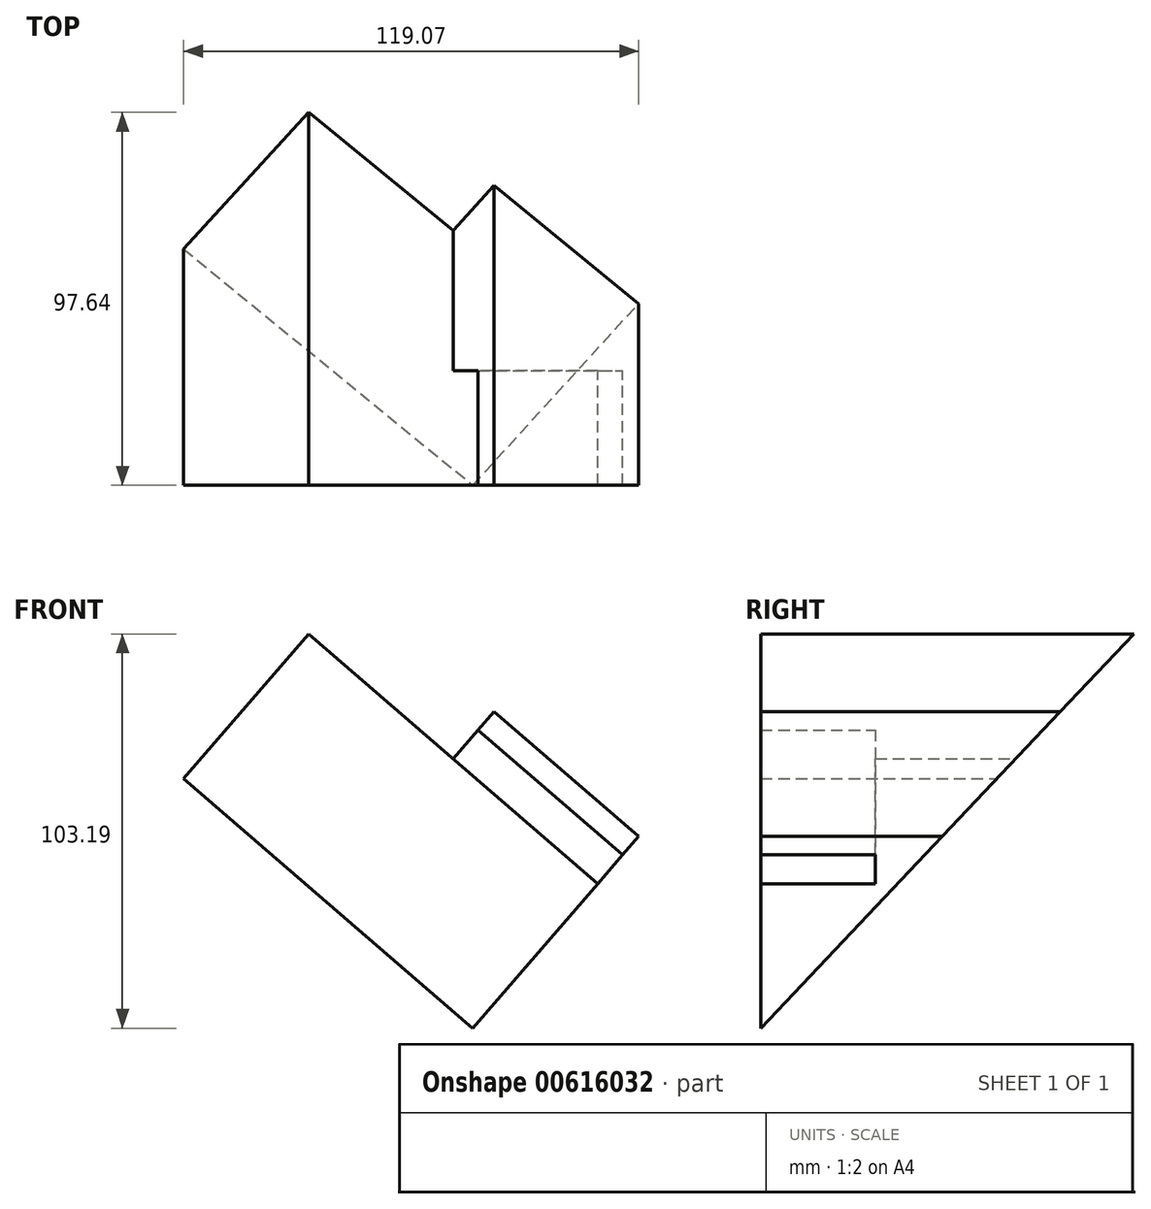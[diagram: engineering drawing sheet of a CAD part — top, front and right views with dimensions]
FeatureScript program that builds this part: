
annotation { "Feature Type Name" : "Feature", "Feature Type Description" : "" }
export const myFeature = defineFeature(function(context is Context, id is Id, definition is map)
    precondition{}
    {
        {
            var Q0;
            Q0=qCreatedBy(makeId("Front.planeOp"),FACE);
            var sketch = newSketch(context, id + "F0", { "sketchPlane" : qUnion([Q0])});
            skLineSegment(sketch, "E0", {"start": v(-8.52, -45.28) * mm, "end": v(24.15, -7.43) * mm});
            skLineSegment(sketch, "E1", {"start": v(24.15, -7.43) * mm, "end": v(-51.55, 57.91) * mm});
            skLineSegment(sketch, "E2", {"start": v(-51.55, 57.91) * mm, "end": v(-84.22, 20.06) * mm});
            skLineSegment(sketch, "E3", {"start": v(-84.22, 20.06) * mm, "end": v(-8.52, -45.28) * mm});
            skLineSegment(sketch, "E4.MirrorCS", {"start": v(47.02, 19.07) * mm, "end": v(30.69, 0.14) * mm});
            skLineSegment(sketch, "E5", {"start": v(44.43, 54.33) * mm, "end": v(44.43, 54.33) * mm});
            skLineSegment(sketch, "E6", {"start": v(9.17, 51.74) * mm, "end": v(-7.16, 32.81) * mm});
            skLineSegment(sketch, "E7", {"start": v(-7.16, 32.81) * mm, "end": v(30.69, 0.14) * mm});
            skPoint(sketch, "E8.visualSharp", {"position": v(25.5, 70.66) * mm});
            skArc(sketch, "E8.filletArc", {"start": v(44.43, 54.33) * mm, "mid": v(26.26, 60.34) * mm, "end": v(9.17, 51.74) * mm});
            skPoint(sketch, "E9.visualSharp", {"position": v(63.36, 38) * mm});
            skArc(sketch, "E9.filletArc", {"start": v(47.02, 19.07) * mm, "mid": v(53.03, 37.23) * mm, "end": v(44.43, 54.33) * mm});
            skLineSegment(sketch, "E10", {"start": v(24.15, -7.43) * mm, "end": v(34.85, 4.96) * mm});
            skLineSegment(sketch, "E11", {"start": v(34.85, 4.96) * mm, "end": v(-3, 37.64) * mm});
            skLineSegment(sketch, "E12", {"start": v(-3, 37.64) * mm, "end": v(-13.7, 25.24) * mm});
            skLineSegment(sketch, "E13", {"start": v(-13.7, 25.24) * mm, "end": v(24.15, -7.43) * mm});
            skSolve(sketch);
        }
        {
            var Q0;
            Q0=qCreatedBy(makeId("Right.planeOp"),FACE);
            var sketch = newSketch(context, id + "F1", { "sketchPlane" : qUnion([Q0])});
            skLineSegment(sketch, "E14", {"start": v(-100, -45.27) * mm, "end": v(0, 60.41) * mm});
            skLineSegment(sketch, "E15", {"start": v(0, 60.41) * mm, "end": v(76.97, -12.42) * mm});
            skLineSegment(sketch, "E16", {"start": v(76.97, -12.42) * mm, "end": v(-18.93, -113.78) * mm});
            skLineSegment(sketch, "E17", {"start": v(-18.93, -113.78) * mm, "end": v(-100, -45.27) * mm});
            skSolve(sketch);
        }
        {
            var Q0;
            {var subQ0=sQuery(id+"F0.wireOp",EDGE,"E7");Q0=makeQuery(id+"F0.imprint","IMPRINT",FACE,{"disambiguationData":[TD([[makeQuery(id+"F0.imprint","IMPRINT",EDGE,{"derivedFrom":subQ0}),-1.0]])]});}
            extrude(context, id + "F2", {"entities" : qUnion([Q0]), "depth" : 70 * mm, "offsetDistance" : 25 * mm});
        }
        {
            var Q0;
            Q0=makeQuery(id+"F0.imprint","IMPRINT",FACE,{"disambiguationData":[TD([[makeQuery(id+"F0.imprint","IMPRINT",EDGE,{"derivedFrom":sQuery(id+"F0.wireOp",EDGE,"E0")}),1.0]])]});
            var Q1;
            Q1=makeQuery(id+"F0.imprint","IMPRINT",FACE,{"disambiguationData":[TD([[makeQuery(id+"F0.imprint","IMPRINT",EDGE,{"derivedFrom":sQuery(id+"F0.wireOp",EDGE,"E4.MirrorCS")}),-1.0]])]});
            var Q2;
            {var subQ0=sQuery(id+"F0.wireOp",EDGE,"E7");Q2=makeQuery(id+"F0.imprint","IMPRINT",FACE,{"disambiguationData":[TD([[makeQuery(id+"F0.imprint","IMPRINT",EDGE,{"derivedFrom":subQ0}),1.0]])]});}
            extrude(context, id + "F3", {"entities" : qUnion([Q0, Q1, Q2]), "operationType" : NewBodyOperationType.ADD, "depth" : 100 * mm, "offsetDistance" : 25 * mm});
        }
        {
            var Q0;
            Q0 = qSketchRegion(id + "F1", true);
            extrude(context, id + "F4", {"entities" : qUnion([Q0]), "operationType" : NewBodyOperationType.REMOVE, "endBound" : BoundingType.SYMMETRIC, "depth" : 200 * mm, "offsetDistance" : 25 * mm});
        }
    });
